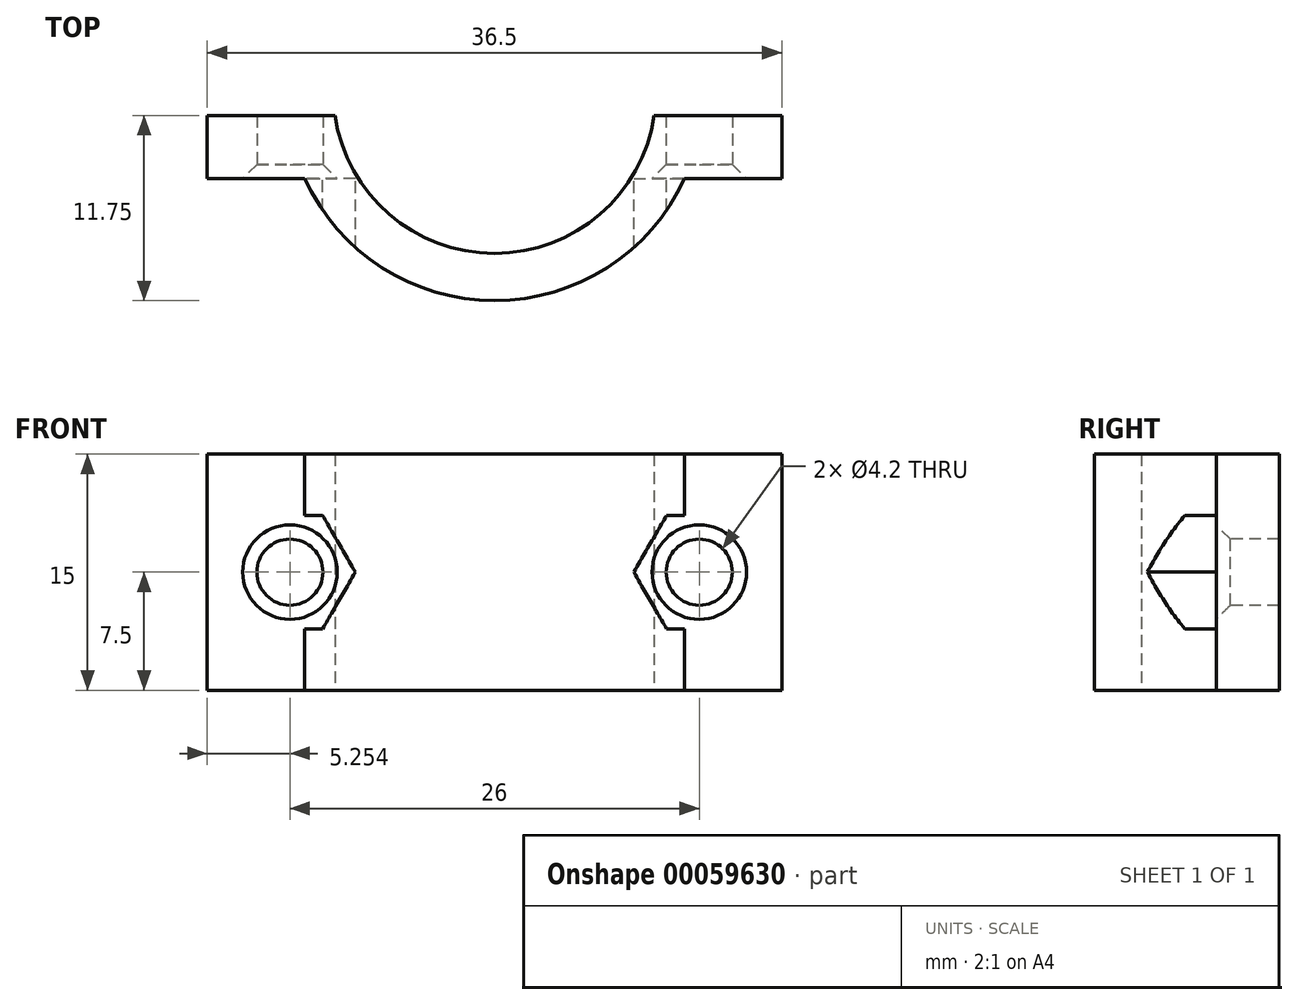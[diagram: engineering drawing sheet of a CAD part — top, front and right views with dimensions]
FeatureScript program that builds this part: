
annotation { "Feature Type Name" : "Feature", "Feature Type Description" : "" }
export const myFeature = defineFeature(function(context is Context, id is Id, definition is map)
    precondition{}
    {
        {
            var Q0;
            Q0=qCreatedBy(makeId("Top.planeOp"),FACE);
            var sketch = newSketch(context, id + "F0", { "sketchPlane" : qUnion([Q0])});
            skCircle(sketch, "E0", {"center": v(-39.82, 35.1) * mm, "radius": 10.25 * mm, "construction": true});
            skLineSegment(sketch, "E1", {"start": v(-50.07, 45.36) * mm, "end": v(-29.57, 45.36) * mm, "construction": true});
            skLineSegment(sketch, "E2", {"start": v(-29.57, 45.36) * mm, "end": v(-29.57, 45.36) * mm});
            skArc(sketch, "E3", {"start": v(-50.07, 45.36) * mm, "mid": v(-39.82, 35.1) * mm, "end": v(-29.57, 45.36) * mm});
            skArc(sketch, "E4", {"start": v(-29.57, 45.36) * mm, "mid": v(-39.82, 55.6) * mm, "end": v(-50.07, 45.36) * mm, "construction": true});
            skLineSegment(sketch, "E5.bottom", {"start": v(-50.07, 45.36) * mm, "end": v(-58.07, 45.36) * mm});
            skLineSegment(sketch, "E5.top", {"start": v(-47.64, 39.86) * mm, "end": v(-58.07, 39.86) * mm});
            skLineSegment(sketch, "E5.right", {"start": v(-58.07, 45.36) * mm, "end": v(-58.07, 39.86) * mm});
            skLineSegment(sketch, "E6.bottom", {"start": v(-29.57, 45.36) * mm, "end": v(-21.57, 45.36) * mm});
            skLineSegment(sketch, "E6.top", {"start": v(-29.41, 39.86) * mm, "end": v(-21.57, 39.86) * mm});
            skLineSegment(sketch, "E6.right", {"start": v(-21.57, 45.36) * mm, "end": v(-21.57, 39.86) * mm});
            skArc(sketch, "E7.0", {"start": v(-53.07, 45.36) * mm, "mid": v(-39.82, 32.1) * mm, "end": v(-26.57, 45.36) * mm});
            skLineSegment(sketch, "E8", {"start": v(-58.07, 43.86) * mm, "end": v(-49.96, 43.86) * mm});
            skLineSegment(sketch, "E9", {"start": v(-49.96, 43.86) * mm, "end": v(-29.68, 43.86) * mm, "construction": true});
            skLineSegment(sketch, "E10", {"start": v(-29.68, 43.86) * mm, "end": v(-21.57, 43.86) * mm});
            skSolve(sketch);
        }
        {
            var Q0;
            {var subQ0=sQuery(id+"F0.wireOp",EDGE,"E8");var subQ1=sQuery(id+"F0.wireOp",EDGE,"E3");var subQ2=makeQuery(id+"F0.imprint","INTERSECT",VERTEX,{"derivedFrom":[subQ1,subQ0]});Q0=makeQuery(id+"F0.imprint","IMPRINT",FACE,{"disambiguationData":[TD([[makeQuery(id+"F0.imprint","IMPRINT",EDGE,{"disambiguationData":[TD([[subQ2,-1.0]])],"derivedFrom":subQ1}),-1.0]])]});}
            var Q1;
            {var subQ0=sQuery(id+"F0.wireOp",EDGE,"E8");var subQ1=sQuery(id+"F0.wireOp",EDGE,"E3");var subQ2=makeQuery(id+"F0.imprint","INTERSECT",VERTEX,{"derivedFrom":[subQ1,subQ0]});Q1=makeQuery(id+"F0.imprint","IMPRINT",FACE,{"disambiguationData":[TD([[makeQuery(id+"F0.imprint","IMPRINT",EDGE,{"disambiguationData":[TD([[subQ2,-1.0]])],"derivedFrom":subQ1}),-1.0]])]});}
            var Q2;
            {var subQ0=sQuery(id+"F0.wireOp",EDGE,"E5.right");var subQ1=sQuery(id+"F0.wireOp",EDGE,"E5.top");var subQ2=makeQuery(id+"F0.imprint","INTERSECT",VERTEX,{"derivedFrom":[subQ1,subQ0]});Q2=makeQuery(id+"F0.imprint","IMPRINT",FACE,{"disambiguationData":[TD([[makeQuery(id+"F0.imprint","IMPRINT",EDGE,{"disambiguationData":[TD([[subQ2,1.0]])],"derivedFrom":subQ1}),-1.0]])]});}
            var Q3;
            {var subQ0=sQuery(id+"F0.wireOp",EDGE,"E6.right");var subQ1=sQuery(id+"F0.wireOp",EDGE,"E6.top");var subQ2=makeQuery(id+"F0.imprint","INTERSECT",VERTEX,{"derivedFrom":[subQ1,subQ0]});Q3=makeQuery(id+"F0.imprint","IMPRINT",FACE,{"disambiguationData":[TD([[makeQuery(id+"F0.imprint","IMPRINT",EDGE,{"disambiguationData":[TD([[subQ2,1.0]])],"derivedFrom":subQ1}),1.0]])]});}
            var Q4;
            {var subQ1=sQuery(id+"F0.wireOp",EDGE,"E3");var subQ6=sQuery(id+"F0.wireOp",EDGE,"E10");var subQ8=makeQuery(id+"F0.imprint","INTERSECT",VERTEX,{"derivedFrom":[subQ1,subQ6]});Q4=makeQuery(id+"F0.imprint","IMPRINT",FACE,{"disambiguationData":[TD([[makeQuery(id+"F0.imprint","IMPRINT",EDGE,{"disambiguationData":[TD([[subQ8,1.0]])],"derivedFrom":subQ1}),-1.0]])]});}
            extrude(context, id + "F1", {"entities" : qUnion([Q0, Q1, Q2, Q3, Q4]), "depth" : 15 * mm});
        }
        {
            var Q0;
            Q0=makeQuery(id+"F1.opExtrude","SWEPT_FACE",FACE,{"disambiguationData":[OSD([sQuery(id+"F0.wireOp",EDGE,"E5.top")])]});
            var sketch = newSketch(context, id + "F2", { "sketchPlane" : qUnion([Q0])});
            skLineSegment(sketch, "E11", {"start": v(-39.82, -4.15) * mm, "end": v(-39.82, 25.65) * mm, "construction": true});
            skLineSegment(sketch, "E12", {"start": v(-58.07, 7.5) * mm, "end": v(-21.57, 7.5) * mm, "construction": true});
            skPoint(sketch, "E11.startSnap0", {"position": v(-39.82, 7.5) * mm});
            skPoint(sketch, "E13", {"position": v(-26.82, 7.5) * mm});
            skPoint(sketch, "E14", {"position": v(-52.82, 7.5) * mm});
            skCircle(sketch, "E15.cCircle", {"center": v(-52.82, 7.5) * mm, "radius": 3.6 * mm, "construction": true});
            skLineSegment(sketch, "E15.0", {"start": v(-50.74, 3.9) * mm, "end": v(-54.9, 3.9) * mm});
            skLineSegment(sketch, "E15.1", {"start": v(-54.9, 3.9) * mm, "end": v(-56.97, 7.5) * mm});
            skLineSegment(sketch, "E15.2", {"start": v(-56.97, 7.5) * mm, "end": v(-54.9, 11.1) * mm});
            skLineSegment(sketch, "E15.3", {"start": v(-54.9, 11.1) * mm, "end": v(-50.74, 11.1) * mm});
            skLineSegment(sketch, "E15.4", {"start": v(-50.74, 11.1) * mm, "end": v(-48.66, 7.5) * mm});
            skLineSegment(sketch, "E15.5", {"start": v(-48.66, 7.5) * mm, "end": v(-50.74, 3.9) * mm});
            skPoint(sketch, "E15.0.midPoint", {"position": v(-52.82, 3.9) * mm});
            skCircle(sketch, "E16.cCircle", {"center": v(-26.82, 7.5) * mm, "radius": 3.6 * mm, "construction": true});
            skLineSegment(sketch, "E16.0", {"start": v(-24.74, 3.9) * mm, "end": v(-28.9, 3.9) * mm});
            skLineSegment(sketch, "E16.1", {"start": v(-28.9, 3.9) * mm, "end": v(-30.97, 7.5) * mm});
            skLineSegment(sketch, "E16.2", {"start": v(-30.97, 7.5) * mm, "end": v(-28.9, 11.1) * mm});
            skLineSegment(sketch, "E16.3", {"start": v(-28.9, 11.1) * mm, "end": v(-24.74, 11.1) * mm});
            skLineSegment(sketch, "E16.4", {"start": v(-24.74, 11.1) * mm, "end": v(-22.66, 7.5) * mm});
            skLineSegment(sketch, "E16.5", {"start": v(-22.66, 7.5) * mm, "end": v(-24.74, 3.9) * mm});
            skPoint(sketch, "E16.0.midPoint", {"position": v(-26.82, 3.9) * mm});
            skSolve(sketch);
        }
        {
            var Q0;
            Q0=sQuery(id+"F2.wireOp",VERTEX,"E14");
            var Q1;
            Q1=sQuery(id+"F2.wireOp",VERTEX,"E13");
            var Q2;
            Q2=makeQuery(id+"F1.opExtrude","SWEPT_BODY",BODY,{"disambiguationData":[OSD([sQuery(id+"F0.wireOp",EDGE,"E3"),sQuery(id+"F0.wireOp",EDGE,"E5.bottom"),sQuery(id+"F0.wireOp",EDGE,"E5.top"),sQuery(id+"F0.wireOp",EDGE,"E5.right"),sQuery(id+"F0.wireOp",EDGE,"E6.bottom"),sQuery(id+"F0.wireOp",EDGE,"E6.top"),sQuery(id+"F0.wireOp",EDGE,"E6.right"),sQuery(id+"F0.wireOp",EDGE,"E7.0")])]});
            hole(context, id + "F3", {"style" : HoleStyle.C_SINK, "holeDiameter" : 4.2 * mm, "cSinkDiameter" : 6 * mm, "endStyle" : HoleEndStyle.BLIND, "holeDepth" : 10 * mm, "locations" : qUnion([Q0, Q1]), "scope" : qUnion([Q2]), "cSinkAngle" : 90 * degree});
        }
        {
            var Q0;
            Q0 = qSketchRegion(id + "F2", true);
            extrude(context, id + "F4", {"entities" : qUnion([Q0]), "operationType" : NewBodyOperationType.REMOVE, "depth" : 25 * mm});
        }
    });
